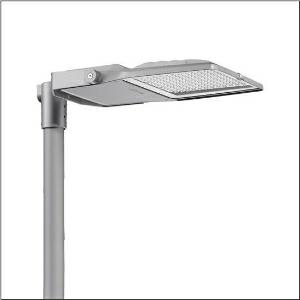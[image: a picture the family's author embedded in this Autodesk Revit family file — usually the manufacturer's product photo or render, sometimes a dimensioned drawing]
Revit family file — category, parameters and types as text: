
# Revit family: floodlight_fl_21_midi___pl52_5xa7786e2d3a_7127
name_source: partatom
category: Lighting Fixtures
units: mm (PartAtom-declared; Revit-internal decimal feet)

## family parameters
Cut with Voids When Loaded = No
Host = Face
Light Source = No
Part Type = Normal
Room Calculation Point = No
Round Connector Dimension = Use Diameter
Shared = No

## types (1)
- --- (1 x LED, 26940 lm, 212.4 W, 3000K)
    Apparent Load = 212 VA
    CIE Flux Codes = 26 60 98 100 100
    Color Rendering = 70
    Color Temperature = 3000K
    Default Elevation = 1800 mm
    Description = Floodlight FL 21 midi, floodlight, primary light control with lens, of PMMA, primary optical cover: protective disc, of toughened safety glass, transparent, light distribution: PL52, light emission: direct distribution, installation type: surface-mounted, LED, High Power LED, rated luminous flux: 26.940lm, luminous efficacy: 127lm/W, light colour: 730, colour temperature: 3000K, control gear: Smart Interface (Zhaga), control: flexible luminous flux parameterisation, time-dependent luminous flux control, constant luminous flux control, overheat protection, pre-setting: logarithmic dimming characteristic, with terminal, 6-pole, mains connection: 220..240V, AC, 50/60Hz, start of lifetime: 212W, end of service life: 231W, reduction: 95W, luminaire housing, of diecast aluminium, powder-coated, SITECO metallic grey (DB 702S), corrosivity category C5 mid according to DIN EN ISO 12944, suitable for swimming pools, chlorine-resistant, sealing non-destructively replaceable, please order mast flange separately, mast bracket, of steel, galvanised, powder-coated, SITECO metallic grey (DB 702S), Smart Interface below and above, protection rating (complete): IP66, insulation class (complete): insulation class II (safety insulation), certification: CE, ENEC, VDE, protection symbol: D, impact resistance: IK08, permissible operating ambient temperature: -40..+40°C, permissible operating ambient temperature for outdoor applications: -40..+50°C, standard: DIN EN 12944, LABS conformity tested according to VDMA 24364:2018-05, packaging unit: 1 piece

Light Distribution: PL52
    Height = 76 mm
    Lamp = 1 x LED
    Lamp Light Flux = 26940 lm
    Lamp Power = 212.4 W
    Lamp count = 1
    Length = 657 mm
    Luminous efficacy = 127 lm/W
    Manufacturer = Siteco
    ModVariant = No
    Model = 5XA7786E2D3A
    Number of Poles = 1
    OnlyDefault = Yes
    Power Factor = 1
    Product Name = Floodlight FL 21 midi | PL52
    Product group = floodlight | pylon annexe
    ProductGroupID = 6201
    Protection Class = Protection class II
    Protection Degree = IP 66
    RLX_Detail_Level = 1
    RLX_Emergency_Light_Flux = 0 lm
    RLX_Emergency_Type = 0
    RLX_Emergency_Type_DB = No
    RlxData = <blob elided: 153717 chars, md5=9930c1f1>
    Socket = socket
    Standby Power = 0 W
    System Light Flux = 26940 lm
    System Power = 212 W
    Type Comments = factory setting: luminous flux: 100 % | dim-lin: 254 | 710 mA
    Type Image = l_1007123.jpg
    URL = http://relux.com
    VarID = @adj_177035
    Voltage = 0 V
    Weight = 0.00 kg
    Width = 442 mm

## geometry (parser evidence)
native form markers: Blend x4, Sweep x14
no freeform markers — native parametric forms only
